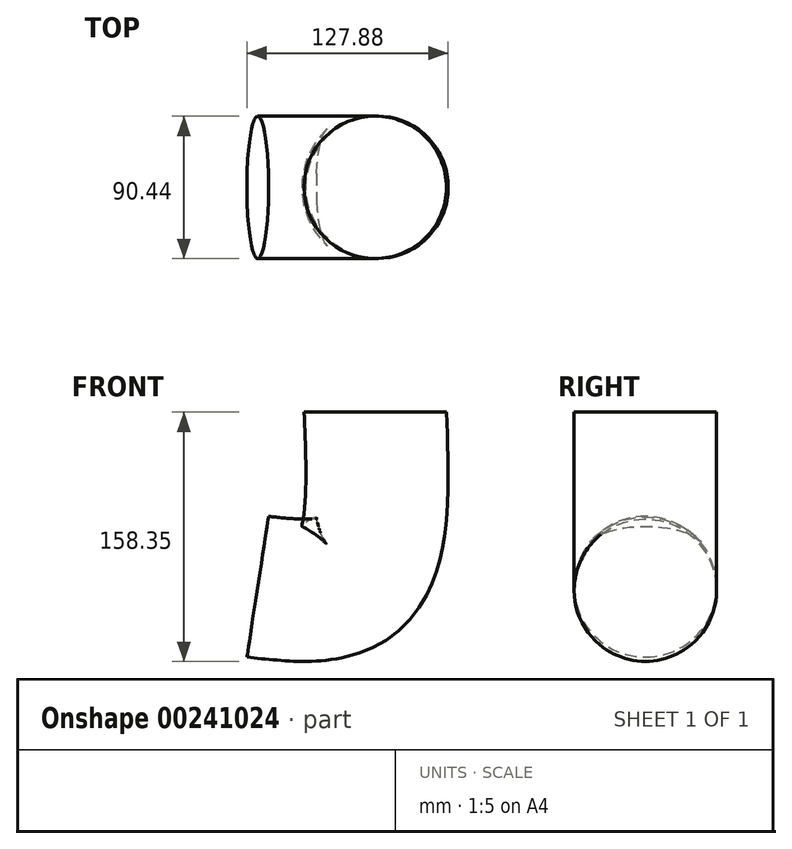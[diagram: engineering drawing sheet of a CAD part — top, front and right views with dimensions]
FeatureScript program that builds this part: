
annotation { "Feature Type Name" : "Feature", "Feature Type Description" : "" }
export const myFeature = defineFeature(function(context is Context, id is Id, definition is map)
    precondition{}
    {
        {
            var Q0;
            Q0=qCreatedBy(makeId("Top.planeOp"),FACE);
            var sketch = newSketch(context, id + "F0", { "sketchPlane" : qUnion([Q0])});
            skCircle(sketch, "E0", {"center": v(0, 0) * mm, "radius": 45.22 * mm});
            skSolve(sketch);
        }
        {
            var Q0;
            Q0=qCreatedBy(makeId("Front.planeOp"),FACE);
            var sketch = newSketch(context, id + "F1", { "sketchPlane" : qUnion([Q0])});
            skFitSpline(sketch, "E1", {"points": [v(0, 0) * mm, v(-13.16, -103.28) * mm, v(-74.62, -110.96) * mm], "startDerivative": vector(9.96, -229.6) * mm, "endDerivative": vector(-166.81, 18.35) * mm});
            skSolve(sketch);
        }
        {
            var Q0;
            Q0=makeQuery(id+"F0.imprint","IMPRINT",FACE,{"disambiguationData":[TD([[makeQuery(id+"F0.imprint","IMPRINT",EDGE,{"derivedFrom":sQuery(id+"F0.wireOp",EDGE,"E0")}),1.0]])]});
            var Q1;
            Q1=sQuery(id+"F1.wireOp",EDGE,"E1");
            sweep(context, id + "F2", {"profiles" : qUnion([Q0]), "path" : qUnion([Q1])});
        }
    });
